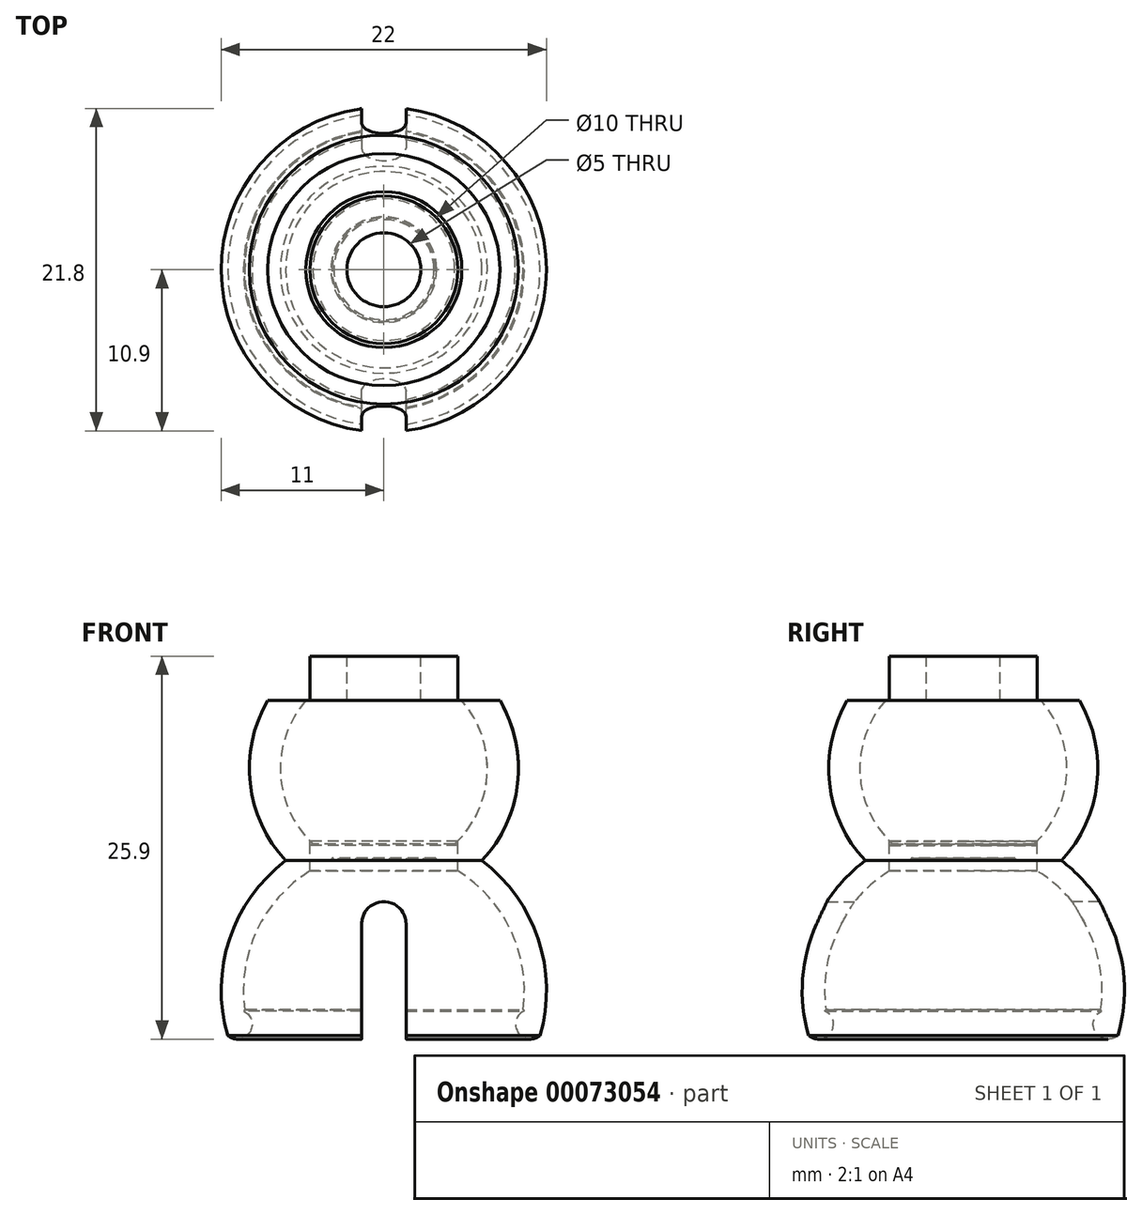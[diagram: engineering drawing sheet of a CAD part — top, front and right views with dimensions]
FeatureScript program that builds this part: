
annotation { "Feature Type Name" : "Feature", "Feature Type Description" : "" }
export const myFeature = defineFeature(function(context is Context, id is Id, definition is map)
    precondition{}
    {
        {
            var Q0;
            Q0=qCreatedBy(makeId("Front.planeOp"),FACE);
            var sketch = newSketch(context, id + "F0", { "sketchPlane" : qUnion([Q0])});
            skCircle(sketch, "E0", {"center": v(0, 0) * mm, "radius": 11 * mm});
            skCircle(sketch, "E1", {"center": v(0, 0) * mm, "radius": 9.5 * mm});
            skCircle(sketch, "E2", {"center": v(0, 15) * mm, "radius": 9.1 * mm});
            skCircle(sketch, "E3", {"center": v(0, 15) * mm, "radius": 7 * mm});
            skLineSegment(sketch, "E4.rect.bottom", {"start": v(5, 5) * mm, "end": v(-5, 5) * mm});
            skLineSegment(sketch, "E4.rect.top", {"start": v(5, 25) * mm, "end": v(-5, 25) * mm});
            skLineSegment(sketch, "E4.rect.left", {"start": v(5, 5) * mm, "end": v(5, 25) * mm});
            skLineSegment(sketch, "E4.rect.right", {"start": v(-5, 5) * mm, "end": v(-5, 25) * mm});
            skCircle(sketch, "E5.cCircle", {"center": v(0, -8) * mm, "radius": 23 * mm, "construction": true});
            skLineSegment(sketch, "E5.0", {"start": v(0, 15) * mm, "end": v(19.92, -19.5) * mm});
            skLineSegment(sketch, "E5.1", {"start": v(19.92, -19.5) * mm, "end": v(-19.92, -19.5) * mm});
            skLineSegment(sketch, "E5.2", {"start": v(-19.92, -19.5) * mm, "end": v(0, 15) * mm});
            skLineSegment(sketch, "E6.rect.bottom", {"start": v(8.41, -21.76) * mm, "end": v(-8.41, -21.76) * mm, "construction": true});
            skLineSegment(sketch, "E6.rect.top", {"start": v(8.41, 21.76) * mm, "end": v(-8.41, 21.76) * mm, "construction": true});
            skLineSegment(sketch, "E6.rect.left", {"start": v(8.41, -21.76) * mm, "end": v(8.41, 21.76) * mm, "construction": true});
            skLineSegment(sketch, "E6.rect.right", {"start": v(-8.41, -21.76) * mm, "end": v(-8.41, 21.76) * mm, "construction": true});
            skLineSegment(sketch, "E7", {"start": v(0, 40.12) * mm, "end": v(0, -47.95) * mm, "construction": true});
            skLineSegment(sketch, "E8.rect.bottom", {"start": v(-7.85, 19.6) * mm, "end": v(7.85, 19.6) * mm});
            skLineSegment(sketch, "E8.rect.top", {"start": v(-7.85, 10.4) * mm, "end": v(7.85, 10.4) * mm});
            skLineSegment(sketch, "E8.rect.left", {"start": v(-7.85, 19.6) * mm, "end": v(-7.85, 10.4) * mm});
            skLineSegment(sketch, "E8.rect.right", {"start": v(7.85, 19.6) * mm, "end": v(7.85, 10.4) * mm});
            skLineSegment(sketch, "E9.bottom", {"start": v(-5, 19.6) * mm, "end": v(5, 19.6) * mm});
            skLineSegment(sketch, "E9.top", {"start": v(-5, 22.6) * mm, "end": v(5, 22.6) * mm});
            skLineSegment(sketch, "E9.left", {"start": v(-5, 19.6) * mm, "end": v(-5, 22.6) * mm});
            skLineSegment(sketch, "E9.right", {"start": v(5, 19.6) * mm, "end": v(5, 22.6) * mm});
            skLineSegment(sketch, "E10.rect.bottom", {"start": v(2.5, 27.1) * mm, "end": v(-2.5, 27.1) * mm});
            skLineSegment(sketch, "E10.rect.top", {"start": v(2.5, 12.1) * mm, "end": v(-2.5, 12.1) * mm});
            skLineSegment(sketch, "E10.rect.left", {"start": v(2.5, 27.1) * mm, "end": v(2.5, 12.1) * mm});
            skLineSegment(sketch, "E10.rect.right", {"start": v(-2.5, 27.1) * mm, "end": v(-2.5, 12.1) * mm});
            skPoint(sketch, "E10.rect.middle", {"position": v(0, 19.6) * mm});
            skCircle(sketch, "E11", {"center": v(-9.91, -2.3) * mm, "radius": 1 * mm});
            skPoint(sketch, "E12", {"position": v(-9.41, -1.3) * mm});
            skSolve(sketch);
        }
        {
            var Q0;
            {var subQ0=sQuery(id+"F0.wireOp",EDGE,"E11");var subQ1=sQuery(id+"F0.wireOp",EDGE,"E1");var subQ2=makeQuery(id+"F0.imprint","INTERSECT",VERTEX,{"disambiguationData":[OD(0.0)],"derivedFrom":[subQ1,subQ0]});Q0=makeQuery(id+"F0.imprint","IMPRINT",FACE,{"disambiguationData":[TD([[makeQuery(id+"F0.imprint","IMPRINT",EDGE,{"disambiguationData":[TD([[subQ2,-1.0]])],"derivedFrom":subQ1}),-1.0]])]});}
            var Q1;
            {var subQ0=sQuery(id+"F0.wireOp",EDGE,"E11");var subQ1=sQuery(id+"F0.wireOp",EDGE,"E0");var subQ2=makeQuery(id+"F0.imprint","INTERSECT",VERTEX,{"disambiguationData":[OD(0.0)],"derivedFrom":[subQ1,subQ0]});Q1=makeQuery(id+"F0.imprint","IMPRINT",FACE,{"disambiguationData":[TD([[makeQuery(id+"F0.imprint","IMPRINT",EDGE,{"disambiguationData":[TD([[subQ2,-1.0]])],"derivedFrom":subQ1}),1.0]])]});}
            var Q2;
            {var subQ0=sQuery(id+"F0.wireOp",EDGE,"E11");var subQ1=sQuery(id+"F0.wireOp",EDGE,"E1");var subQ2=makeQuery(id+"F0.imprint","INTERSECT",VERTEX,{"disambiguationData":[OD(0.0)],"derivedFrom":[subQ1,subQ0]});Q2=makeQuery(id+"F0.imprint","IMPRINT",FACE,{"disambiguationData":[TD([[makeQuery(id+"F0.imprint","IMPRINT",EDGE,{"disambiguationData":[TD([[subQ2,-1.0]])],"derivedFrom":subQ1}),1.0]])]});}
            var Q3;
            {var subQ5=sQuery(id+"F0.wireOp",EDGE,"E0");var subQ7=sQuery(id+"F0.wireOp",EDGE,"E2");var subQ8=makeQuery(id+"F0.imprint","INTERSECT",VERTEX,{"disambiguationData":[OD(1.0)],"derivedFrom":[subQ5,subQ7]});Q3=makeQuery(id+"F0.imprint","IMPRINT",FACE,{"disambiguationData":[TD([[makeQuery(id+"F0.imprint","IMPRINT",EDGE,{"disambiguationData":[TD([[subQ8,-1.0]])],"derivedFrom":subQ5}),1.0]])]});}
            var Q4;
            {var subQ0=sQuery(id+"F0.wireOp",EDGE,"E2");var subQ1=sQuery(id+"F0.wireOp",EDGE,"E0");var subQ2=makeQuery(id+"F0.imprint","INTERSECT",VERTEX,{"disambiguationData":[OD(1.0)],"derivedFrom":[subQ1,subQ0]});Q4=makeQuery(id+"F0.imprint","IMPRINT",FACE,{"disambiguationData":[TD([[makeQuery(id+"F0.imprint","IMPRINT",EDGE,{"disambiguationData":[TD([[subQ2,1.0]])],"derivedFrom":subQ1}),1.0]])]});}
            var Q5;
            {var subQ5=sQuery(id+"F0.wireOp",EDGE,"E8.rect.left");Q5=makeQuery(id+"F0.imprint","IMPRINT",FACE,{"disambiguationData":[TD([[makeQuery(id+"F0.imprint","IMPRINT",EDGE,{"derivedFrom":subQ5}),1.0]])]});}
            var Q6;
            {var subQ0=sQuery(id+"F0.wireOp",EDGE,"E8.rect.left");Q6=makeQuery(id+"F0.imprint","IMPRINT",FACE,{"disambiguationData":[TD([[makeQuery(id+"F0.imprint","IMPRINT",EDGE,{"derivedFrom":subQ0}),-1.0]])]});}
            var Q7;
            {var subQ3=sQuery(id+"F0.wireOp",EDGE,"E9.left");var subQ5=sQuery(id+"F0.wireOp",EDGE,"E3");var subQ6=makeQuery(id+"F0.imprint","INTERSECT",VERTEX,{"derivedFrom":[subQ5,subQ3]});Q7=makeQuery(id+"F0.imprint","IMPRINT",FACE,{"disambiguationData":[TD([[makeQuery(id+"F0.imprint","IMPRINT",EDGE,{"disambiguationData":[TD([[subQ6,-1.0]])],"derivedFrom":subQ5}),-1.0]])]});}
            var Q8;
            {var subQ0=sQuery(id+"F0.wireOp",EDGE,"E10.rect.right");var subQ1=sQuery(id+"F0.wireOp",EDGE,"E3");var subQ2=makeQuery(id+"F0.imprint","INTERSECT",VERTEX,{"derivedFrom":[subQ1,subQ0]});Q8=makeQuery(id+"F0.imprint","IMPRINT",FACE,{"disambiguationData":[TD([[makeQuery(id+"F0.imprint","IMPRINT",EDGE,{"disambiguationData":[TD([[subQ2,-1.0]])],"derivedFrom":subQ1}),-1.0]])]});}
            var Q9;
            {var subQ0=sQuery(id+"F0.wireOp",EDGE,"E10.rect.right");var subQ1=sQuery(id+"F0.wireOp",EDGE,"E3");var subQ2=makeQuery(id+"F0.imprint","INTERSECT",VERTEX,{"derivedFrom":[subQ1,subQ0]});Q9=makeQuery(id+"F0.imprint","IMPRINT",FACE,{"disambiguationData":[TD([[makeQuery(id+"F0.imprint","IMPRINT",EDGE,{"disambiguationData":[TD([[subQ2,-1.0]])],"derivedFrom":subQ1}),1.0]])]});}
            var Q10;
            {var subQ1=sQuery(id+"F0.wireOp",EDGE,"E0");var subQ6=sQuery(id+"F0.wireOp",EDGE,"E2");var subQ9=makeQuery(id+"F0.imprint","INTERSECT",VERTEX,{"disambiguationData":[OD(1.0)],"derivedFrom":[subQ1,subQ6]});Q10=makeQuery(id+"F0.imprint","IMPRINT",FACE,{"disambiguationData":[TD([[makeQuery(id+"F0.imprint","IMPRINT",EDGE,{"disambiguationData":[TD([[subQ9,1.0]])],"derivedFrom":subQ1}),-1.0]])]});}
            var Q11;
            Q11=sQuery(id+"F0.wireOp",EDGE,"E7");
            revolve(context, id + "F1", {"entities" : qUnion([Q0, Q1, Q2, Q3, Q4, Q5, Q6, Q7, Q8, Q9, Q10]), "axis" : qUnion([Q11]), "revolveType" : RevolveType.FULL});
        }
        {
            var Q0;
            Q0=qCreatedBy(makeId("Front.planeOp"),FACE);
            var sketch = newSketch(context, id + "F2", { "sketchPlane" : qUnion([Q0])});
            skLineSegment(sketch, "E13.rect.bottom", {"start": v(1.5, -5) * mm, "end": v(-1.5, -5) * mm});
            skLineSegment(sketch, "E13.rect.top", {"start": v(0, 6) * mm, "end": v(0, 6) * mm});
            skLineSegment(sketch, "E13.rect.left", {"start": v(1.5, -5) * mm, "end": v(1.5, 4.5) * mm});
            skLineSegment(sketch, "E13.rect.right", {"start": v(-1.5, -5) * mm, "end": v(-1.5, 4.5) * mm});
            skPoint(sketch, "E13.rect.middle", {"position": v(0, 0.5) * mm});
            skPoint(sketch, "E14.visualSharp", {"position": v(1.5, 6) * mm});
            skArc(sketch, "E14.filletArc", {"start": v(1.5, 4.5) * mm, "mid": v(1.06, 5.56) * mm, "end": v(0, 6) * mm});
            skPoint(sketch, "E15.visualSharp", {"position": v(-1.5, 6) * mm});
            skArc(sketch, "E15.filletArc", {"start": v(0, 6) * mm, "mid": v(-1.06, 5.56) * mm, "end": v(-1.5, 4.5) * mm});
            skSolve(sketch);
        }
        {
            var Q0;
            Q0 = qSketchRegion(id + "F2", true);
            extrude(context, id + "F3", {"entities" : qUnion([Q0]), "operationType" : NewBodyOperationType.REMOVE, "oppositeDirection" : true, "depth" : 25 * mm});
        }
        {
            var Q0;
            Q0 = qSketchRegion(id + "F2", true);
            extrude(context, id + "F4", {"entities" : qUnion([Q0]), "operationType" : NewBodyOperationType.REMOVE, "depth" : 25 * mm});
        }
    });
